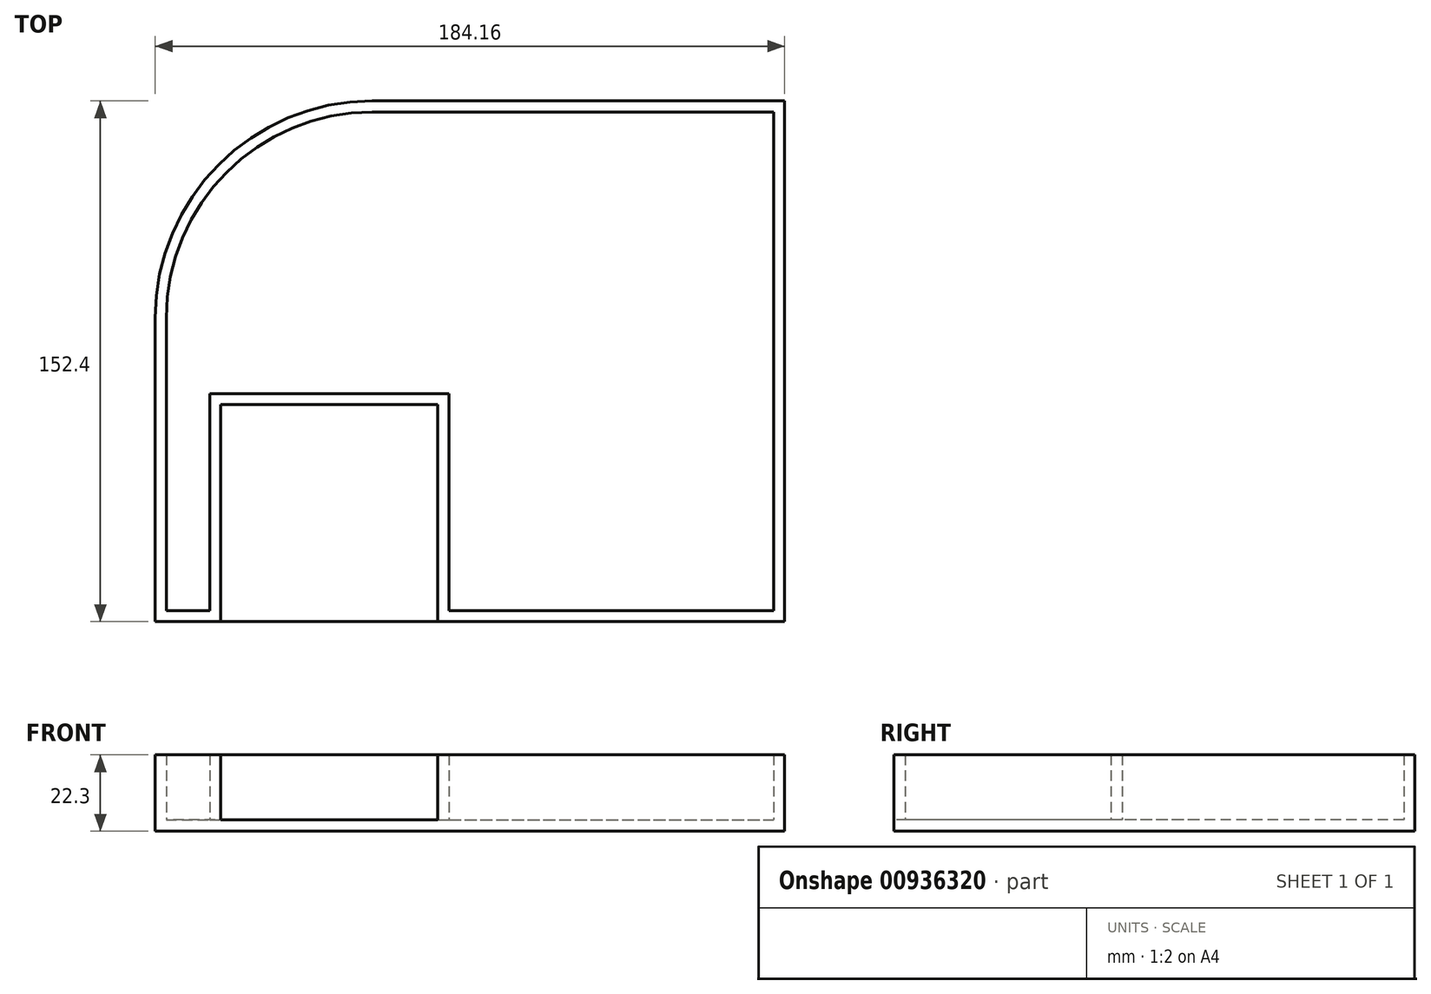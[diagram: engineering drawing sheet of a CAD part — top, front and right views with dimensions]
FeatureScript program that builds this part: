
annotation { "Feature Type Name" : "Feature", "Feature Type Description" : "" }
export const myFeature = defineFeature(function(context is Context, id is Id, definition is map)
    precondition{}
    {
        {
            var Q0;
            Q0=qCreatedBy(makeId("Top.planeOp"),FACE);
            var sketch = newSketch(context, id + "F0", { "sketchPlane" : qUnion([Q0])});
            skLineSegment(sketch, "E0.bottom", {"start": v(-28.57, 76.2) * mm, "end": v(92.08, 76.2) * mm});
            skLineSegment(sketch, "E0.left", {"start": v(-92.08, 12.7) * mm, "end": v(-92.08, -76.2) * mm});
            skLineSegment(sketch, "E0.right", {"start": v(92.08, 76.2) * mm, "end": v(92.07, -76.2) * mm});
            skPoint(sketch, "E0.middle", {"position": v(0, 0) * mm});
            skPoint(sketch, "E1.visualSharp", {"position": v(-92.07, 76.2) * mm});
            skArc(sketch, "E1.filletArc", {"start": v(-28.57, 76.2) * mm, "mid": v(-73.48, 57.6) * mm, "end": v(-92.07, 12.7) * mm});
            skLineSegment(sketch, "E2", {"start": v(-92.08, -76.2) * mm, "end": v(92.07, -76.2) * mm});
            skSolve(sketch);
        }
        {
            var Q0;
            Q0=makeQuery(id+"F0.imprint","IMPRINT",FACE,{"disambiguationData":[TD([[makeQuery(id+"F0.imprint","IMPRINT",EDGE,{"derivedFrom":sQuery(id+"F0.wireOp",EDGE,"E0.bottom")}),-1.0]])]});
            extrude(context, id + "F1", {"entities" : qUnion([Q0]), "depth" : 3.25 * mm, "offsetDistance" : 25.4 * mm});
        }
        {
            var Q0;
            Q0=makeQuery(id+"F1.opExtrude","CAP_FACE",FACE,{"disambiguationData":[OSD([sQuery(id+"F0.wireOp",EDGE,"E0.bottom"),sQuery(id+"F0.wireOp",EDGE,"E0.left"),sQuery(id+"F0.wireOp",EDGE,"E0.right"),sQuery(id+"F0.wireOp",EDGE,"E1.filletArc"),sQuery(id+"F0.wireOp",EDGE,"E2")])],"isStart":false});
            var sketch = newSketch(context, id + "F2", { "sketchPlane" : qUnion([Q0])});
            skLineSegment(sketch, "E3.0", {"start": v(88.82, 72.95) * mm, "end": v(88.82, -72.95) * mm});
            skLineSegment(sketch, "E3.1", {"start": v(-28.57, 72.95) * mm, "end": v(88.82, 72.95) * mm});
            skLineSegment(sketch, "E3.2", {"start": v(-88.82, -72.95) * mm, "end": v(-76.12, -72.95) * mm});
            skLineSegment(sketch, "E3.3", {"start": v(-88.82, 12.7) * mm, "end": v(-88.82, -72.95) * mm});
            skArc(sketch, "E3.4", {"start": v(-28.57, 72.95) * mm, "mid": v(-71.18, 55.3) * mm, "end": v(-88.82, 12.7) * mm});
            skLineSegment(sketch, "E4.bottom", {"start": v(-72.87, -12.7) * mm, "end": v(-9.37, -12.7) * mm});
            skLineSegment(sketch, "E4.left", {"start": v(-72.87, -12.7) * mm, "end": v(-72.87, -76.2) * mm});
            skLineSegment(sketch, "E4.right", {"start": v(-9.37, -12.7) * mm, "end": v(-9.37, -76.2) * mm});
            skLineSegment(sketch, "E5.0", {"start": v(-6.12, -9.45) * mm, "end": v(-6.12, -72.95) * mm});
            skLineSegment(sketch, "E5.1", {"start": v(-76.12, -9.45) * mm, "end": v(-6.12, -9.45) * mm});
            skLineSegment(sketch, "E5.2", {"start": v(-76.12, -9.45) * mm, "end": v(-76.12, -72.95) * mm});
            skPoint(sketch, "E6", {"position": v(-6.12, -72.95) * mm});
            skPoint(sketch, "E7", {"position": v(-76.12, -72.95) * mm});
            skLineSegment(sketch, "E8", {"start": v(-72.87, -76.2) * mm, "end": v(-9.37, -76.2) * mm});
            skPoint(sketch, "E9", {"position": v(-72.87, -72.95) * mm});
            skPoint(sketch, "E10", {"position": v(-9.37, -72.95) * mm});
            skLineSegment(sketch, "E11.trimOffspring", {"start": v(-6.12, -72.95) * mm, "end": v(88.82, -72.95) * mm});
            skSolve(sketch);
        }
        {
            var Q0;
            Q0=makeQuery(id+"F2.imprint","IMPRINT",FACE,{"disambiguationData":[TD([[makeQuery(id+"F2.imprint","IMPRINT",EDGE,{"derivedFrom":sQuery(id+"F2.wireOp",EDGE,"E3.0")}),1.0]])]});
            extrude(context, id + "F3", {"entities" : qUnion([Q0]), "operationType" : NewBodyOperationType.ADD, "depth" : 19.05 * mm, "offsetDistance" : 25.4 * mm});
        }
    });
